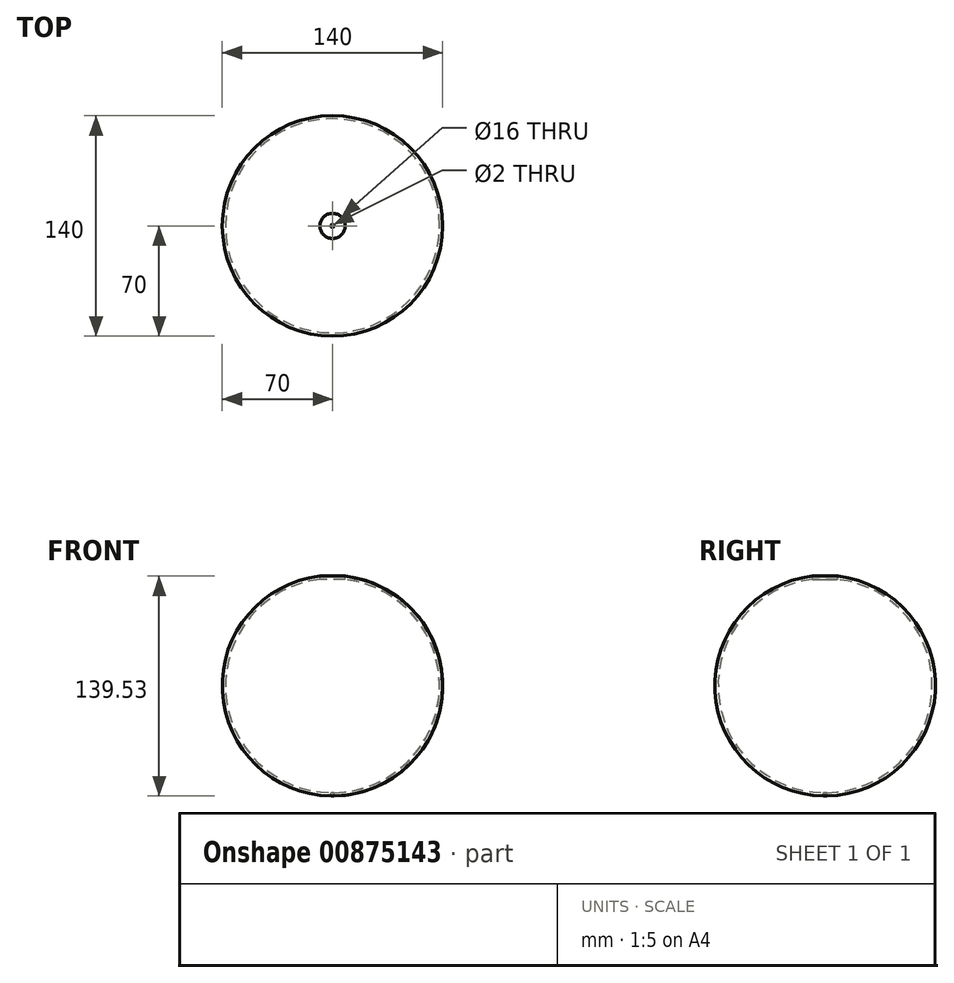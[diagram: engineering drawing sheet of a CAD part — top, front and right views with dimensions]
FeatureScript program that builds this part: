
annotation { "Feature Type Name" : "Feature", "Feature Type Description" : "" }
export const myFeature = defineFeature(function(context is Context, id is Id, definition is map)
    precondition{}
    {
        {
            var Q0;
            Q0=qCreatedBy(makeId("Front.planeOp"),FACE);
            var sketch = newSketch(context, id + "F0", { "sketchPlane" : qUnion([Q0])});
            skArc(sketch, "E0", {"start": v(0, 70) * mm, "mid": v(-70, 0) * mm, "end": v(0, -70) * mm});
            skLineSegment(sketch, "E1", {"start": v(0, 98.7) * mm, "end": v(0, -118.58) * mm, "construction": true});
            skArc(sketch, "E2.0", {"start": v(0, 68) * mm, "mid": v(-68, 0) * mm, "end": v(0, -68) * mm});
            skLineSegment(sketch, "E3.trimOffspring", {"start": v(-1, -68) * mm, "end": v(-1, -70) * mm});
            skLineSegment(sketch, "E4", {"start": v(-8, 69.54) * mm, "end": v(-8, 67.53) * mm});
            skSolve(sketch);
        }
        {
            var Q0;
            Q0 = qSketchRegion(id + "F0", true);
            var Q1;
            Q1=sQuery(id+"F0.wireOp",EDGE,"E1");
            revolve(context, id + "F1", {"surfaceOperationType" : NewSurfaceOperationType.NEW, "entities" : qUnion([Q0]), "axis" : qUnion([Q1]), "revolveType" : RevolveType.FULL});
        }
    });
